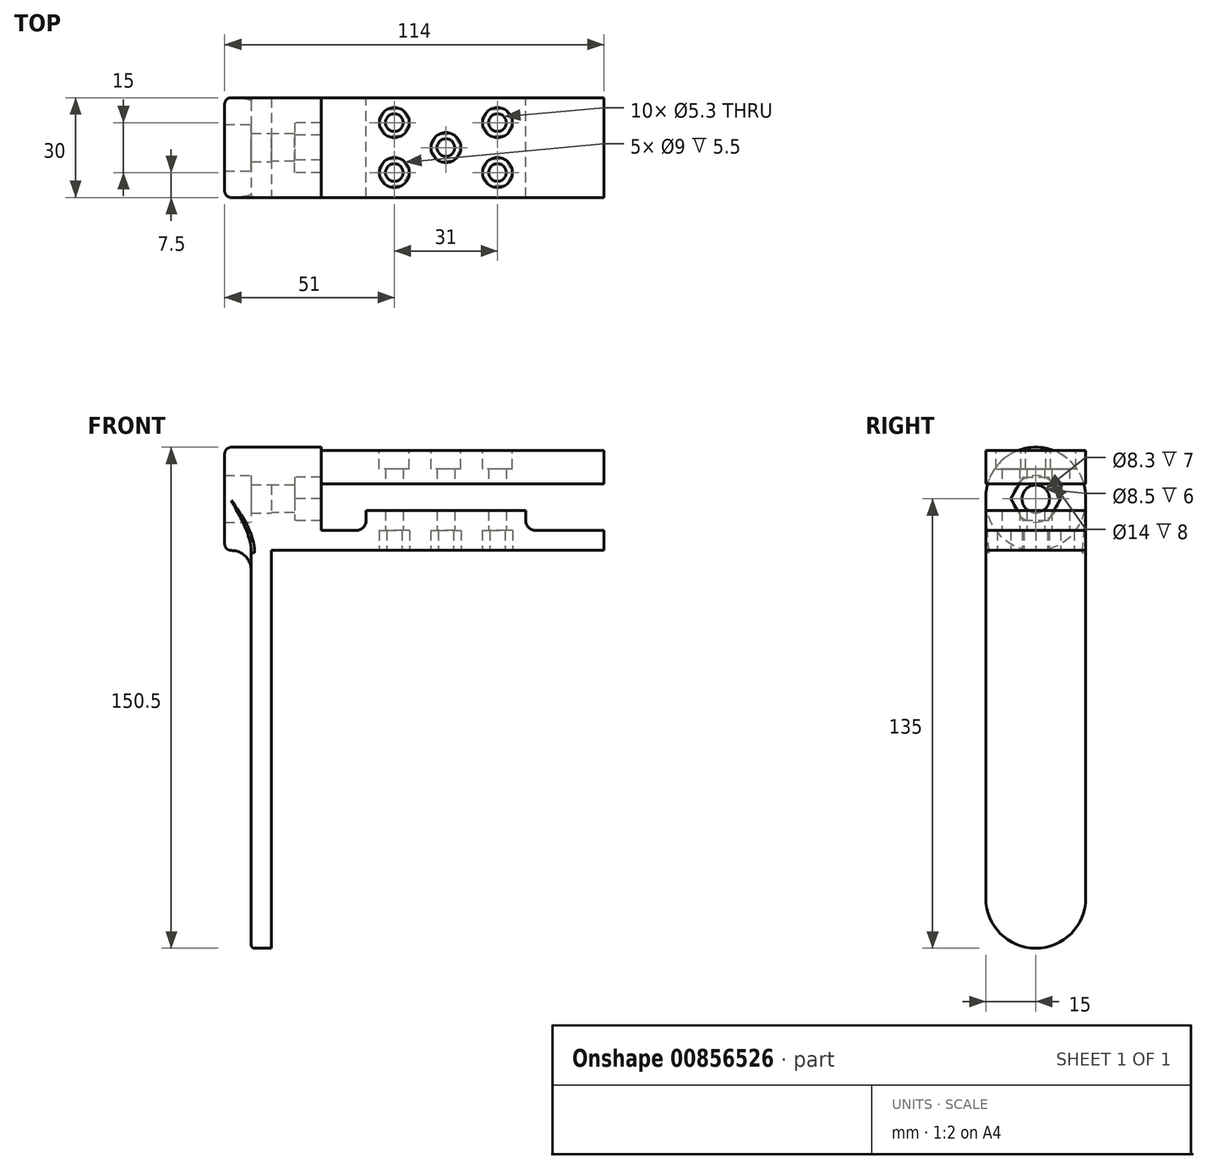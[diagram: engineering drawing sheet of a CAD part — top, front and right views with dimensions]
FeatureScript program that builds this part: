
annotation { "Feature Type Name" : "Feature", "Feature Type Description" : "" }
export const myFeature = defineFeature(function(context is Context, id is Id, definition is map)
    precondition{}
    {
        {
            var Q0;
            Q0=qCreatedBy(makeId("Top.planeOp"),FACE);
            var sketch = newSketch(context, id + "F0", { "sketchPlane" : qUnion([Q0])});
            skLineSegment(sketch, "E0.bottom", {"start": v(-50, 15) * mm, "end": v(50, 15) * mm});
            skLineSegment(sketch, "E0.top", {"start": v(-50, -15) * mm, "end": v(50, -15) * mm});
            skLineSegment(sketch, "E0.left", {"start": v(-50, 15) * mm, "end": v(-50, -15) * mm});
            skLineSegment(sketch, "E0.right", {"start": v(50, 15) * mm, "end": v(50, -15) * mm});
            skLineSegment(sketch, "E1", {"start": v(-35, 15) * mm, "end": v(-35, -15) * mm});
            skCircle(sketch, "E2", {"center": v(-13, 7.5) * mm, "radius": 2.65 * mm});
            skCircle(sketch, "E3", {"center": v(18, 7.5) * mm, "radius": 2.65 * mm});
            skCircle(sketch, "E4", {"center": v(18, -7.5) * mm, "radius": 2.65 * mm});
            skCircle(sketch, "E5", {"center": v(-13, -7.5) * mm, "radius": 2.65 * mm});
            skCircle(sketch, "E6", {"center": v(2.5, 0) * mm, "radius": 2.65 * mm});
            skLineSegment(sketch, "E7.bottom", {"start": v(-21.5, 15) * mm, "end": v(26.5, 15) * mm});
            skLineSegment(sketch, "E7.top", {"start": v(-21.5, -15) * mm, "end": v(26.5, -15) * mm});
            skLineSegment(sketch, "E7.left", {"start": v(-21.5, 15) * mm, "end": v(-21.5, -15) * mm});
            skLineSegment(sketch, "E7.right", {"start": v(26.5, 15) * mm, "end": v(26.5, -15) * mm});
            skCircle(sketch, "E8.cCircle", {"center": v(-13, 7.5) * mm, "radius": 4 * mm, "construction": true});
            skLineSegment(sketch, "E8.0", {"start": v(-10.7, 3.5) * mm, "end": v(-15.3, 3.5) * mm});
            skLineSegment(sketch, "E8.1", {"start": v(-15.3, 3.5) * mm, "end": v(-17.62, 7.5) * mm});
            skLineSegment(sketch, "E8.2", {"start": v(-17.62, 7.5) * mm, "end": v(-15.3, 11.5) * mm});
            skLineSegment(sketch, "E8.3", {"start": v(-15.3, 11.5) * mm, "end": v(-10.7, 11.5) * mm});
            skLineSegment(sketch, "E8.4", {"start": v(-10.7, 11.5) * mm, "end": v(-8.38, 7.5) * mm});
            skLineSegment(sketch, "E8.5", {"start": v(-8.38, 7.5) * mm, "end": v(-10.7, 3.5) * mm});
            skPoint(sketch, "E8.0.midPoint", {"position": v(-13, 3.5) * mm});
            skCircle(sketch, "E9.cCircle", {"center": v(18, 7.5) * mm, "radius": 4 * mm, "construction": true});
            skLineSegment(sketch, "E9.0", {"start": v(20.3, 3.5) * mm, "end": v(15.7, 3.5) * mm});
            skLineSegment(sketch, "E9.1", {"start": v(15.7, 3.5) * mm, "end": v(13.38, 7.5) * mm});
            skLineSegment(sketch, "E9.2", {"start": v(13.38, 7.5) * mm, "end": v(15.7, 11.5) * mm});
            skLineSegment(sketch, "E9.3", {"start": v(15.7, 11.5) * mm, "end": v(20.3, 11.5) * mm});
            skLineSegment(sketch, "E9.4", {"start": v(20.3, 11.5) * mm, "end": v(22.62, 7.5) * mm});
            skLineSegment(sketch, "E9.5", {"start": v(22.62, 7.5) * mm, "end": v(20.3, 3.5) * mm});
            skPoint(sketch, "E9.0.midPoint", {"position": v(18, 3.5) * mm});
            skCircle(sketch, "E10.cCircle", {"center": v(-13, -7.5) * mm, "radius": 4 * mm, "construction": true});
            skLineSegment(sketch, "E10.0", {"start": v(-15.3, -3.5) * mm, "end": v(-10.7, -3.5) * mm});
            skLineSegment(sketch, "E10.1", {"start": v(-10.7, -3.5) * mm, "end": v(-8.38, -7.5) * mm});
            skLineSegment(sketch, "E10.2", {"start": v(-8.38, -7.5) * mm, "end": v(-10.7, -11.5) * mm});
            skLineSegment(sketch, "E10.3", {"start": v(-10.7, -11.5) * mm, "end": v(-15.3, -11.5) * mm});
            skLineSegment(sketch, "E10.4", {"start": v(-15.3, -11.5) * mm, "end": v(-17.62, -7.5) * mm});
            skLineSegment(sketch, "E10.5", {"start": v(-17.62, -7.5) * mm, "end": v(-15.3, -3.5) * mm});
            skPoint(sketch, "E10.0.midPoint", {"position": v(-13, -3.5) * mm});
            skCircle(sketch, "E11.cCircle", {"center": v(18, -7.5) * mm, "radius": 4 * mm, "construction": true});
            skLineSegment(sketch, "E11.0", {"start": v(15.7, -3.5) * mm, "end": v(20.3, -3.5) * mm});
            skLineSegment(sketch, "E11.1", {"start": v(20.3, -3.5) * mm, "end": v(22.62, -7.5) * mm});
            skLineSegment(sketch, "E11.2", {"start": v(22.62, -7.5) * mm, "end": v(20.3, -11.5) * mm});
            skLineSegment(sketch, "E11.3", {"start": v(20.3, -11.5) * mm, "end": v(15.7, -11.5) * mm});
            skLineSegment(sketch, "E11.4", {"start": v(15.7, -11.5) * mm, "end": v(13.38, -7.5) * mm});
            skLineSegment(sketch, "E11.5", {"start": v(13.38, -7.5) * mm, "end": v(15.7, -3.5) * mm});
            skPoint(sketch, "E11.0.midPoint", {"position": v(18, -3.5) * mm});
            skCircle(sketch, "E12.cCircle", {"center": v(2.5, 0) * mm, "radius": 4 * mm, "construction": true});
            skLineSegment(sketch, "E12.0", {"start": v(4.8, 4) * mm, "end": v(7.12, 0) * mm});
            skLineSegment(sketch, "E12.1", {"start": v(7.12, 0) * mm, "end": v(4.8, -4) * mm});
            skLineSegment(sketch, "E12.2", {"start": v(4.8, -4) * mm, "end": v(0.2, -4) * mm});
            skLineSegment(sketch, "E12.3", {"start": v(0.2, -4) * mm, "end": v(-2.12, 0) * mm});
            skLineSegment(sketch, "E12.4", {"start": v(-2.12, 0) * mm, "end": v(0.2, 4) * mm});
            skLineSegment(sketch, "E12.5", {"start": v(0.2, 4) * mm, "end": v(4.8, 4) * mm});
            skPoint(sketch, "E12.0.midPoint", {"position": v(5.96, 2) * mm});
            skSolve(sketch);
        }
        {
            var Q0;
            {var subQ0=sQuery(id+"F0.wireOp",EDGE,"E0.right");Q0=makeQuery(id+"F0.imprint","IMPRINT",FACE,{"disambiguationData":[TD([[makeQuery(id+"F0.imprint","IMPRINT",EDGE,{"derivedFrom":subQ0}),-1.0]])]});}
            var Q1;
            {var subQ2=sQuery(id+"F0.wireOp",EDGE,"E1");Q1=makeQuery(id+"F0.imprint","IMPRINT",FACE,{"disambiguationData":[TD([[makeQuery(id+"F0.imprint","IMPRINT",EDGE,{"derivedFrom":subQ2}),1.0]])]});}
            var Q2;
            Q2=makeQuery(id+"F0.imprint","IMPRINT",FACE,{"disambiguationData":[TD([[makeQuery(id+"F0.imprint","IMPRINT",EDGE,{"derivedFrom":sQuery(id+"F0.wireOp",EDGE,"E2")}),-1.0]])]});
            var Q3;
            Q3=makeQuery(id+"F0.imprint","IMPRINT",FACE,{"disambiguationData":[TD([[makeQuery(id+"F0.imprint","IMPRINT",EDGE,{"derivedFrom":sQuery(id+"F0.wireOp",EDGE,"E5")}),-1.0]])]});
            var Q4;
            Q4=makeQuery(id+"F0.imprint","IMPRINT",FACE,{"disambiguationData":[TD([[makeQuery(id+"F0.imprint","IMPRINT",EDGE,{"derivedFrom":sQuery(id+"F0.wireOp",EDGE,"E6")}),-1.0]])]});
            var Q5;
            Q5=makeQuery(id+"F0.imprint","IMPRINT",FACE,{"disambiguationData":[TD([[makeQuery(id+"F0.imprint","IMPRINT",EDGE,{"derivedFrom":sQuery(id+"F0.wireOp",EDGE,"E3")}),-1.0]])]});
            var Q6;
            {var subQ1=sQuery(id+"F0.wireOp",EDGE,"E7.left");Q6=makeQuery(id+"F0.imprint","IMPRINT",FACE,{"disambiguationData":[TD([[makeQuery(id+"F0.imprint","IMPRINT",EDGE,{"derivedFrom":subQ1}),1.0]])]});}
            var Q7;
            Q7=makeQuery(id+"F0.imprint","IMPRINT",FACE,{"disambiguationData":[TD([[makeQuery(id+"F0.imprint","IMPRINT",EDGE,{"derivedFrom":sQuery(id+"F0.wireOp",EDGE,"E4")}),-1.0]])]});
            extrude(context, id + "F1", {"entities" : qUnion([Q0, Q1, Q2, Q3, Q4, Q5, Q6, Q7]), "depth" : 6 * mm, "offsetDistance" : 25 * mm});
        }
        {
            var Q0;
            {var subQ1=sQuery(id+"F0.wireOp",EDGE,"E7.left");Q0=makeQuery(id+"F0.imprint","IMPRINT",FACE,{"disambiguationData":[TD([[makeQuery(id+"F0.imprint","IMPRINT",EDGE,{"derivedFrom":subQ1}),1.0]])]});}
            var Q1;
            Q1=makeQuery(id+"F0.imprint","IMPRINT",FACE,{"disambiguationData":[TD([[makeQuery(id+"F0.imprint","IMPRINT",EDGE,{"derivedFrom":sQuery(id+"F0.wireOp",EDGE,"E2")}),-1.0]])]});
            var Q2;
            Q2=makeQuery(id+"F0.imprint","IMPRINT",FACE,{"disambiguationData":[TD([[makeQuery(id+"F0.imprint","IMPRINT",EDGE,{"derivedFrom":sQuery(id+"F0.wireOp",EDGE,"E5")}),-1.0]])]});
            var Q3;
            Q3=makeQuery(id+"F0.imprint","IMPRINT",FACE,{"disambiguationData":[TD([[makeQuery(id+"F0.imprint","IMPRINT",EDGE,{"derivedFrom":sQuery(id+"F0.wireOp",EDGE,"E6")}),-1.0]])]});
            var Q4;
            Q4=makeQuery(id+"F0.imprint","IMPRINT",FACE,{"disambiguationData":[TD([[makeQuery(id+"F0.imprint","IMPRINT",EDGE,{"derivedFrom":sQuery(id+"F0.wireOp",EDGE,"E3")}),-1.0]])]});
            var Q5;
            Q5=makeQuery(id+"F0.imprint","IMPRINT",FACE,{"disambiguationData":[TD([[makeQuery(id+"F0.imprint","IMPRINT",EDGE,{"derivedFrom":sQuery(id+"F0.wireOp",EDGE,"E4")}),-1.0]])]});
            extrude(context, id + "F2", {"entities" : qUnion([Q0, Q1, Q2, Q3, Q4, Q5]), "operationType" : NewBodyOperationType.ADD, "depth" : 12 * mm, "offsetDistance" : 25 * mm});
        }
        {
            var Q0;
            Q0=makeQuery(id+"F0.imprint","IMPRINT",FACE,{"disambiguationData":[TD([[makeQuery(id+"F0.imprint","IMPRINT",EDGE,{"derivedFrom":sQuery(id+"F0.wireOp",EDGE,"E5")}),-1.0]])]});
            var Q1;
            Q1=makeQuery(id+"F0.imprint","IMPRINT",FACE,{"disambiguationData":[TD([[makeQuery(id+"F0.imprint","IMPRINT",EDGE,{"derivedFrom":sQuery(id+"F0.wireOp",EDGE,"E2")}),-1.0]])]});
            var Q2;
            Q2=makeQuery(id+"F0.imprint","IMPRINT",FACE,{"disambiguationData":[TD([[makeQuery(id+"F0.imprint","IMPRINT",EDGE,{"derivedFrom":sQuery(id+"F0.wireOp",EDGE,"E6")}),-1.0]])]});
            var Q3;
            Q3=makeQuery(id+"F0.imprint","IMPRINT",FACE,{"disambiguationData":[TD([[makeQuery(id+"F0.imprint","IMPRINT",EDGE,{"derivedFrom":sQuery(id+"F0.wireOp",EDGE,"E4")}),-1.0]])]});
            var Q4;
            Q4=makeQuery(id+"F0.imprint","IMPRINT",FACE,{"disambiguationData":[TD([[makeQuery(id+"F0.imprint","IMPRINT",EDGE,{"derivedFrom":sQuery(id+"F0.wireOp",EDGE,"E3")}),-1.0]])]});
            extrude(context, id + "F3", {"entities" : qUnion([Q0, Q1, Q2, Q3, Q4]), "operationType" : NewBodyOperationType.REMOVE, "depth" : 6 * mm, "offsetDistance" : 25 * mm});
        }
        {
            var Q0;
            {var subQ0=sQuery(id+"F0.wireOp",EDGE,"E0.left");Q0=makeQuery(id+"F0.imprint","IMPRINT",FACE,{"disambiguationData":[TD([[makeQuery(id+"F0.imprint","IMPRINT",EDGE,{"derivedFrom":subQ0}),1.0]])]});}
            extrude(context, id + "F4", {"entities" : qUnion([Q0]), "operationType" : NewBodyOperationType.ADD, "depth" : 31 * mm, "offsetDistance" : 25 * mm});
        }
        {
            var Q0;
            Q0=makeQuery(id+"F1.opExtrude","CAP_EDGE",EDGE,{"disambiguationData":[OSD([sQuery(id+"F0.wireOp",EDGE,"E1")])],"isStart":false});
            var Q1;
            Q1=makeQuery(id+"F2.boolean.opBoolean","INTERSECT",EDGE,{"derivedFrom":[makeQuery(id+"F1.opExtrude","CAP_FACE",FACE,{"disambiguationData":[OSD([sQuery(id+"F0.wireOp",EDGE,"E0.bottom"),sQuery(id+"F0.wireOp",EDGE,"E0.top"),sQuery(id+"F0.wireOp",EDGE,"E0.right"),sQuery(id+"F0.wireOp",EDGE,"E1"),sQuery(id+"F0.wireOp",EDGE,"E2"),sQuery(id+"F0.wireOp",EDGE,"E3"),sQuery(id+"F0.wireOp",EDGE,"E4"),sQuery(id+"F0.wireOp",EDGE,"E5"),sQuery(id+"F0.wireOp",EDGE,"E6")])],"isStart":false}),makeQuery(id+"F2.opExtrude","SWEPT_FACE",FACE,{"disambiguationData":[OSD([sQuery(id+"F0.wireOp",EDGE,"E7.right")])]})]});
            var Q2;
            Q2=makeQuery(id+"F2.boolean.opBoolean","INTERSECT",EDGE,{"derivedFrom":[makeQuery(id+"F1.opExtrude","CAP_FACE",FACE,{"disambiguationData":[OSD([sQuery(id+"F0.wireOp",EDGE,"E0.bottom"),sQuery(id+"F0.wireOp",EDGE,"E0.top"),sQuery(id+"F0.wireOp",EDGE,"E0.right"),sQuery(id+"F0.wireOp",EDGE,"E1"),sQuery(id+"F0.wireOp",EDGE,"E2"),sQuery(id+"F0.wireOp",EDGE,"E3"),sQuery(id+"F0.wireOp",EDGE,"E4"),sQuery(id+"F0.wireOp",EDGE,"E5"),sQuery(id+"F0.wireOp",EDGE,"E6")])],"isStart":false}),makeQuery(id+"F2.opExtrude","SWEPT_FACE",FACE,{"disambiguationData":[OSD([sQuery(id+"F0.wireOp",EDGE,"E7.left")])]})]});
            fillet(context, id + "F5", {"entities" : qUnion([Q0, Q1, Q2]), "radius" : 3 * mm, "tangentPropagation" : true, "allowEdgeOverflow" : false});
        }
        {
            var Q0;
            Q0=makeQuery(id+"F4.opExtrude","SWEPT_FACE",FACE,{"disambiguationData":[OSD([sQuery(id+"F0.wireOp",EDGE,"E0.left")])]});
            var sketch = newSketch(context, id + "F6", { "sketchPlane" : qUnion([Q0])});
            skLineSegment(sketch, "E13", {"start": v(-15, 31) * mm, "end": v(15, 0) * mm});
            skCircle(sketch, "E14", {"center": v(0, 15.5) * mm, "radius": 4.15 * mm});
            skCircle(sketch, "E15.cCircle", {"center": v(0, 15.5) * mm, "radius": 6.5 * mm, "construction": true});
            skLineSegment(sketch, "E15.0", {"start": v(3.75, 9) * mm, "end": v(-3.75, 9) * mm});
            skLineSegment(sketch, "E15.1", {"start": v(-3.75, 9) * mm, "end": v(-7.5, 15.5) * mm});
            skLineSegment(sketch, "E15.2", {"start": v(-7.5, 15.5) * mm, "end": v(-3.75, 22) * mm});
            skLineSegment(sketch, "E15.3", {"start": v(-3.75, 22) * mm, "end": v(3.75, 22) * mm});
            skLineSegment(sketch, "E15.4", {"start": v(3.75, 22) * mm, "end": v(7.5, 15.5) * mm});
            skLineSegment(sketch, "E15.5", {"start": v(7.5, 15.5) * mm, "end": v(3.75, 9) * mm});
            skPoint(sketch, "E15.0.midPoint", {"position": v(0, 9) * mm});
            skSolve(sketch);
        }
        {
            var Q0;
            {var subQ0=sQuery(id+"F6.wireOp",EDGE,"E14");var subQ1=sQuery(id+"F6.wireOp",EDGE,"E13");var subQ2=makeQuery(id+"F6.imprint","INTERSECT",VERTEX,{"disambiguationData":[OD(0.0)],"derivedFrom":[subQ1,subQ0]});Q0=makeQuery(id+"F6.imprint","IMPRINT",FACE,{"disambiguationData":[TD([[makeQuery(id+"F6.imprint","IMPRINT",EDGE,{"disambiguationData":[TD([[subQ2,-1.0]])],"derivedFrom":subQ1}),1.0]])]});}
            var Q1;
            {var subQ0=sQuery(id+"F6.wireOp",EDGE,"E14");var subQ1=sQuery(id+"F6.wireOp",EDGE,"E13");var subQ2=makeQuery(id+"F6.imprint","INTERSECT",VERTEX,{"disambiguationData":[OD(0.0)],"derivedFrom":[subQ1,subQ0]});Q1=makeQuery(id+"F6.imprint","IMPRINT",FACE,{"disambiguationData":[TD([[makeQuery(id+"F6.imprint","IMPRINT",EDGE,{"disambiguationData":[TD([[subQ2,-1.0]])],"derivedFrom":subQ1}),-1.0]])]});}
            extrude(context, id + "F7", {"entities" : qUnion([Q0, Q1]), "operationType" : NewBodyOperationType.REMOVE, "oppositeDirection" : true, "depth" : 20 * mm, "offsetDistance" : 25 * mm});
        }
        {
            var Q0;
            Q0 = qSketchRegion(id + "F6", true);
            extrude(context, id + "F8", {"entities" : qUnion([Q0]), "operationType" : NewBodyOperationType.REMOVE, "oppositeDirection" : true, "depth" : 20 * mm, "offsetDistance" : 25 * mm, "hasSecondDirection" : true, "secondDirectionOppositeDirection" : true, "secondDirectionDepth" : 7 * mm});
        }
        {
            var Q0;
            Q0=makeQuery(id+"F4.opExtrude","CAP_EDGE",EDGE,{"disambiguationData":[OSD([sQuery(id+"F0.wireOp",EDGE,"E0.top")])],"isStart":false});
            var Q1;
            Q1=makeQuery(id+"F4.opExtrude","CAP_EDGE",EDGE,{"disambiguationData":[OSD([sQuery(id+"F0.wireOp",EDGE,"E0.bottom")])],"isStart":false});
            fillet(context, id + "F9", {"entities" : qUnion([Q0, Q1]), "radius" : 15 * mm, "tangentPropagation" : true, "allowEdgeOverflow" : false});
        }
        {
            var Q0;
            {var subQ2=sQuery(id+"F0.wireOp",EDGE,"E1");Q0=makeQuery(id+"F0.imprint","IMPRINT",FACE,{"disambiguationData":[TD([[makeQuery(id+"F0.imprint","IMPRINT",EDGE,{"derivedFrom":subQ2}),1.0]])]});}
            var Q1;
            {var subQ1=sQuery(id+"F0.wireOp",EDGE,"E7.left");Q1=makeQuery(id+"F0.imprint","IMPRINT",FACE,{"disambiguationData":[TD([[makeQuery(id+"F0.imprint","IMPRINT",EDGE,{"derivedFrom":subQ1}),1.0]])]});}
            var Q2;
            {var subQ0=sQuery(id+"F0.wireOp",EDGE,"E0.right");Q2=makeQuery(id+"F0.imprint","IMPRINT",FACE,{"disambiguationData":[TD([[makeQuery(id+"F0.imprint","IMPRINT",EDGE,{"derivedFrom":subQ0}),-1.0]])]});}
            var Q3;
            Q3=makeQuery(id+"F0.imprint","IMPRINT",FACE,{"disambiguationData":[TD([[makeQuery(id+"F0.imprint","IMPRINT",EDGE,{"derivedFrom":sQuery(id+"F0.wireOp",EDGE,"E4")}),-1.0]])]});
            var Q4;
            Q4=makeQuery(id+"F0.imprint","IMPRINT",FACE,{"disambiguationData":[TD([[makeQuery(id+"F0.imprint","IMPRINT",EDGE,{"derivedFrom":sQuery(id+"F0.wireOp",EDGE,"E3")}),-1.0]])]});
            var Q5;
            Q5=makeQuery(id+"F0.imprint","IMPRINT",FACE,{"disambiguationData":[TD([[makeQuery(id+"F0.imprint","IMPRINT",EDGE,{"derivedFrom":sQuery(id+"F0.wireOp",EDGE,"E6")}),-1.0]])]});
            var Q6;
            Q6=makeQuery(id+"F0.imprint","IMPRINT",FACE,{"disambiguationData":[TD([[makeQuery(id+"F0.imprint","IMPRINT",EDGE,{"derivedFrom":sQuery(id+"F0.wireOp",EDGE,"E5")}),-1.0]])]});
            var Q7;
            Q7=makeQuery(id+"F0.imprint","IMPRINT",FACE,{"disambiguationData":[TD([[makeQuery(id+"F0.imprint","IMPRINT",EDGE,{"derivedFrom":sQuery(id+"F0.wireOp",EDGE,"E2")}),-1.0]])]});
            extrude(context, id + "F10", {"entities" : qUnion([Q0, Q1, Q2, Q3, Q4, Q5, Q6, Q7]), "depth" : 30 * mm, "offsetDistance" : 25 * mm, "hasSecondDirection" : true, "secondDirectionOppositeDirection" : false, "secondDirectionDepth" : 20 * mm});
        }
        {
            var Q0;
            Q0=makeQuery(id+"F10.opExtrude","CAP_FACE",FACE,{"disambiguationData":[OSD([sQuery(id+"F0.wireOp",EDGE,"E0.bottom"),sQuery(id+"F0.wireOp",EDGE,"E0.top"),sQuery(id+"F0.wireOp",EDGE,"E0.right"),sQuery(id+"F0.wireOp",EDGE,"E1"),sQuery(id+"F0.wireOp",EDGE,"E2"),sQuery(id+"F0.wireOp",EDGE,"E3"),sQuery(id+"F0.wireOp",EDGE,"E4"),sQuery(id+"F0.wireOp",EDGE,"E5"),sQuery(id+"F0.wireOp",EDGE,"E6")])],"isStart":false});
            var sketch = newSketch(context, id + "F11", { "sketchPlane" : qUnion([Q0])});
            skCircle(sketch, "E16", {"center": v(-13, 7.5) * mm, "radius": 4.5 * mm});
            skCircle(sketch, "E17", {"center": v(18, 7.5) * mm, "radius": 4.5 * mm});
            skCircle(sketch, "E18", {"center": v(18, -7.5) * mm, "radius": 4.5 * mm});
            skCircle(sketch, "E19", {"center": v(-13, -7.5) * mm, "radius": 4.5 * mm});
            skCircle(sketch, "E20", {"center": v(2.5, 0) * mm, "radius": 4.5 * mm});
            skSolve(sketch);
        }
        {
            var Q0;
            Q0=makeQuery(id+"F11.imprint","IMPRINT",FACE,{"disambiguationData":[TD([[makeQuery(id+"F11.imprint","IMPRINT",EDGE,{"derivedFrom":sQuery(id+"F11.wireOp",EDGE,"E16")}),1.0]])]});
            var Q1;
            Q1=makeQuery(id+"F11.imprint","IMPRINT",FACE,{"disambiguationData":[TD([[makeQuery(id+"F11.imprint","IMPRINT",EDGE,{"derivedFrom":sQuery(id+"F11.wireOp",EDGE,"E19")}),1.0]])]});
            var Q2;
            Q2=makeQuery(id+"F11.imprint","IMPRINT",FACE,{"disambiguationData":[TD([[makeQuery(id+"F11.imprint","IMPRINT",EDGE,{"derivedFrom":sQuery(id+"F11.wireOp",EDGE,"E17")}),1.0]])]});
            var Q3;
            Q3=makeQuery(id+"F11.imprint","IMPRINT",FACE,{"disambiguationData":[TD([[makeQuery(id+"F11.imprint","IMPRINT",EDGE,{"derivedFrom":sQuery(id+"F11.wireOp",EDGE,"E18")}),1.0]])]});
            var Q4;
            Q4=makeQuery(id+"F11.imprint","IMPRINT",FACE,{"disambiguationData":[TD([[makeQuery(id+"F11.imprint","IMPRINT",EDGE,{"derivedFrom":sQuery(id+"F11.wireOp",EDGE,"E20")}),1.0]])]});
            extrude(context, id + "F12", {"entities" : qUnion([Q0, Q1, Q2, Q3, Q4]), "operationType" : NewBodyOperationType.REMOVE, "oppositeDirection" : true, "depth" : 5.5 * mm, "offsetDistance" : 25 * mm});
        }
        {
            var Q0;
            Q0=makeQuery(id+"F4.opExtrude","SWEPT_FACE",FACE,{"disambiguationData":[OSD([sQuery(id+"F0.wireOp",EDGE,"E0.left")])]});
            var sketch = newSketch(context, id + "F13", { "sketchPlane" : qUnion([Q0])});
            skLineSegment(sketch, "E21.bottom", {"start": v(-15, 31) * mm, "end": v(15, 31) * mm});
            skLineSegment(sketch, "E21.top", {"start": v(0, -119.5) * mm, "end": v(0, -119.5) * mm});
            skLineSegment(sketch, "E21.left", {"start": v(-15, 31) * mm, "end": v(-15, -104.5) * mm});
            skLineSegment(sketch, "E21.right", {"start": v(15, 31) * mm, "end": v(15, -104.5) * mm});
            skCircle(sketch, "E22", {"center": v(0, 15.5) * mm, "radius": 4.25 * mm});
            skCircle(sketch, "E23", {"center": v(0, 15.5) * mm, "radius": 7 * mm});
            skPoint(sketch, "E24.visualSharp", {"position": v(15, -119.5) * mm});
            skArc(sketch, "E24.filletArc", {"start": v(0, -119.5) * mm, "mid": v(10.6, -115.1) * mm, "end": v(15, -104.5) * mm});
            skPoint(sketch, "E25.visualSharp", {"position": v(-15, -119.5) * mm});
            skArc(sketch, "E25.filletArc", {"start": v(-15, -104.5) * mm, "mid": v(-10.6, -115.1) * mm, "end": v(0, -119.5) * mm});
            skLineSegment(sketch, "E26", {"start": v(-15, 0) * mm, "end": v(15, 0) * mm});
            skSolve(sketch);
        }
        {
            var Q0;
            Q0=makeQuery(id+"F13.imprint","IMPRINT",FACE,{"disambiguationData":[TD([[makeQuery(id+"F13.imprint","IMPRINT",EDGE,{"derivedFrom":sQuery(id+"F13.wireOp",EDGE,"E23")}),-1.0]])]});
            var Q1;
            {var subQ0=sQuery(id+"F13.wireOp",EDGE,"E24.filletArc");Q1=makeQuery(id+"F13.imprint","IMPRINT",FACE,{"disambiguationData":[TD([[makeQuery(id+"F13.imprint","IMPRINT",EDGE,{"derivedFrom":subQ0}),1.0]])]});}
            var Q2;
            Q2=makeQuery(id+"F13.imprint","IMPRINT",FACE,{"disambiguationData":[TD([[makeQuery(id+"F13.imprint","IMPRINT",EDGE,{"derivedFrom":sQuery(id+"F13.wireOp",EDGE,"E22")}),-1.0]])]});
            extrude(context, id + "F14", {"entities" : qUnion([Q0, Q1, Q2]), "depth" : 6 * mm, "offsetDistance" : 25 * mm});
        }
        {
            var Q0;
            Q0=makeQuery(id+"F13.imprint","IMPRINT",FACE,{"disambiguationData":[TD([[makeQuery(id+"F13.imprint","IMPRINT",EDGE,{"derivedFrom":sQuery(id+"F13.wireOp",EDGE,"E23")}),-1.0]])]});
            extrude(context, id + "F15", {"entities" : qUnion([Q0]), "operationType" : NewBodyOperationType.ADD, "depth" : (8 + 6) * mm, "offsetDistance" : 25 * mm});
        }
        {
            var Q0;
            Q0=makeQuery(id+"F15.opExtrude","SWEPT_EDGE",EDGE,{"disambiguationData":[OSD([sQuery(id+"F13.wireOp",EDGE,"E21.left"),sQuery(id+"F13.wireOp",EDGE,"E26")])]});
            var Q1;
            Q1=makeQuery(id+"F15.opExtrude","SWEPT_EDGE",EDGE,{"disambiguationData":[OSD([sQuery(id+"F13.wireOp",EDGE,"E21.right"),sQuery(id+"F13.wireOp",EDGE,"E26")])]});
            fillet(context, id + "F16", {"entities" : qUnion([Q0, Q1]), "radius" : 15 * mm, "allowEdgeOverflow" : false});
        }
        {
            var Q0;
            {var subQ0=sQuery(id+"F13.wireOp",EDGE,"E21.left");var subQ1=sQuery(id+"F13.wireOp",EDGE,"E21.right");var subQ2=sQuery(id+"F13.wireOp",EDGE,"E25.filletArc");var subQ3=sQuery(id+"F13.wireOp",EDGE,"E24.filletArc");var subQ4=sQuery(id+"F13.wireOp",EDGE,"E26");Q0=makeQuery(id+"F16.opFillet","BLEND_EDGE",EDGE,{"blendedFrom":[makeQuery(id+"F15.opExtrude","SWEPT_EDGE",EDGE,{"disambiguationData":[OSD([subQ0,subQ4])]}),makeQuery(id+"F15.boolean.opBoolean","SPLIT",FACE,{"disambiguationData":[TD([makeQuery(id+"F14.opExtrude","SWEPT_FACE",FACE,{"disambiguationData":[OSD([subQ0])]})])],"derivedFrom":makeQuery(id+"F14.opExtrude","CAP_FACE",FACE,{"disambiguationData":[OSD([sQuery(id+"F0.wireOp",EDGE,"E0.bottom"),sQuery(id+"F0.wireOp",EDGE,"E0.left"),subQ0,subQ1,sQuery(id+"F13.wireOp",EDGE,"E22"),subQ3,subQ2])],"isStart":false})})],"blendedInto":[makeQuery(id+"F15.boolean.opBoolean","SPLIT",FACE,{"disambiguationData":[TD([makeQuery(id+"F14.opExtrude","SWEPT_FACE",FACE,{"disambiguationData":[OSD([subQ0])]})])],"derivedFrom":makeQuery(id+"F14.opExtrude","CAP_FACE",FACE,{"disambiguationData":[OSD([sQuery(id+"F0.wireOp",EDGE,"E0.bottom"),sQuery(id+"F0.wireOp",EDGE,"E0.left"),subQ0,subQ1,sQuery(id+"F13.wireOp",EDGE,"E22"),subQ3,subQ2])],"isStart":false})})]});}
            fillet(context, id + "F17", {"entities" : qUnion([Q0]), "radius" : 6 * mm, "tangentPropagation" : true, "allowEdgeOverflow" : false});
        }
        {
            var Q0;
            {var subQ0=sQuery(id+"F13.wireOp",EDGE,"E26");var subQ1=sQuery(id+"F13.wireOp",EDGE,"E21.left");Q0=makeQuery(id+"F16.opFillet","BLEND_EDGE",EDGE,{"blendedFrom":[makeQuery(id+"F15.opExtrude","SWEPT_EDGE",EDGE,{"disambiguationData":[OSD([subQ1,subQ0])]}),makeQuery(id+"F15.opExtrude","CAP_FACE",FACE,{"disambiguationData":[OSD([sQuery(id+"F0.wireOp",EDGE,"E0.bottom"),sQuery(id+"F0.wireOp",EDGE,"E0.left"),subQ1,sQuery(id+"F13.wireOp",EDGE,"E21.right"),sQuery(id+"F13.wireOp",EDGE,"E23"),subQ0])],"isStart":false})],"blendedInto":[makeQuery(id+"F15.opExtrude","CAP_FACE",FACE,{"disambiguationData":[OSD([sQuery(id+"F0.wireOp",EDGE,"E0.bottom"),sQuery(id+"F0.wireOp",EDGE,"E0.left"),subQ1,sQuery(id+"F13.wireOp",EDGE,"E21.right"),sQuery(id+"F13.wireOp",EDGE,"E23"),subQ0])],"isStart":false})]});}
            fillet(context, id + "F18", {"entities" : qUnion([Q0]), "radius" : 2 * mm, "tangentPropagation" : true, "allowEdgeOverflow" : false});
        }
        {
            var Q0;
            Q0=makeQuery(id+"F14.opExtrude","CAP_EDGE",EDGE,{"disambiguationData":[OSD([sQuery(id+"F13.wireOp",EDGE,"E21.right")])],"isStart":false});
            fillet(context, id + "F19", {"entities" : qUnion([Q0]), "radius" : 1 * mm, "tangentPropagation" : true, "allowEdgeOverflow" : false});
        }
    });
